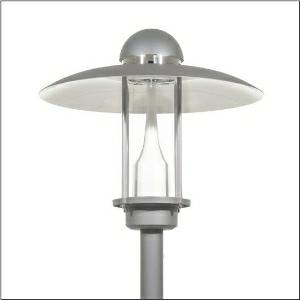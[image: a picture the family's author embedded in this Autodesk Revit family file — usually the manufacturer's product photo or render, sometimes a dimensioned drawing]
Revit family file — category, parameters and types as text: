
# Revit family: city-light_elegance_iq___st1_2a_5xa5265af14hp_6ffd
name_source: partatom
category: Lighting Fixtures
units: mm (PartAtom-declared; Revit-internal decimal feet)

## family parameters
Cut with Voids When Loaded = No
Host = Face
Light Source = No
Part Type = Normal
Room Calculation Point = No
Round Connector Dimension = Use Diameter
Shared = No

## types (1)
- --- (1 x LED, 3730 lm, 33.6 W, 2200K)
    Apparent Load = 34 VA
    CIE Flux Codes = 22 61 93 98 100
    Color Rendering = 70
    Color Temperature = 2200K
    Default Elevation = 1800 mm
    Description = City-Light Elegance iQ, mast luminaire, Module 540 iQ-SR, primary light control with 3 zone facetted reflector, of plastic, silver coated, highly specular, structured, primary optical cover: cover, of PMMA, transparent, light distribution: ST1.2a, light emission: direct distribution, primary light characteristic: asymmetric, installation type: post-top, LED, High Power LED, rated luminous flux: 3.730lm, luminous efficacy: 111lm/W, light colour: 722, colour temperature: 2200K, control gear: iQ Street-Remote, control: pre-setting: logarithmic dimming characteristic, Street-Remote, Auto-Match, Temp-Guard, Lumen-Switch, Night-Set, Smart-Wire, Light-Fading, Desk-Remote (wireless, voltage-free reading and setting of iQ features in the workshop via application-optimized NFC function/RFID function), optimised constant luminous flux control (CLO 2.0), with terminal, 6-pole, max. 2.5mm², mains connection: 230..240V, AC, 50/60Hz, start of lifetime: 34W, end of service life: 36W, reduction: 15W, luminaire housing, upper part, of aluminium, coated, Siteco® metallic grey (DB 702S), diameter: 750mm, height: 675mm, spigot size: d x l = 76 x 70mm (post-top) | with reducer (optional accessory) 60 x 70mm, mounting height: 3..5m, post-top mast mounting element, of diecast aluminium, coated, Siteco® metallic grey (DB 702S), Module 540 iQ-SR, traffic white (RAL 9016), equipment: Power, protection rating (complete): IP65, insulation class (complete): insulation class II (safety insulation), certification: CE, ENEC, VDE, packaging unit: 1 piece

Light Distribution: ST1.2a
    Height = 675 mm
    Lamp = 1 x LED
    Lamp Light Flux = 3730 lm
    Lamp Power = 33.6 W
    Lamp count = 1
    Length = 750 mm
    Luminous efficacy = 111 lm/W
    Manufacturer = Siteco
    ModVariant = No
    Model = 5XA5265AF14HP
    Number of Poles = 1
    OnlyDefault = Yes
    Power Factor = 1
    Product Name = City-Light Elegance iQ | ST1.2a
    Product group = mast luminaire | pylon top
    ProductGroupID = 6100
    Protection Class = Protection class II
    Protection Degree = IP 65
    RLX_Detail_Level = 1
    RLX_Emergency_Light_Flux = 0 lm
    RLX_Emergency_Type = 0
    RLX_Emergency_Type_DB = No
    RlxData = <blob elided: 36633 chars, md5=2f897dc0>
    Socket = socket
    Standby Power = 0 W
    System Light Flux = 3730 lm
    System Power = 34 W
    Type Comments = factory setting: luminous flux: 100 % | dim-lin: 254 | 695 mA
    Type Image = l_1006912.jpg
    URL = http://relux.com
    VarID = @adj_214389
    Voltage = 0 V
    Weight = 0.00 kg
    Width = 0 mm  [stored 0 ft]

note: [stored X ft] marks values corroborated as IEEE doubles in the binary element streams (Revit-internal decimal feet)

## geometry (parser evidence)
native form markers: Blend x4, Sweep x9
no freeform markers — native parametric forms only
